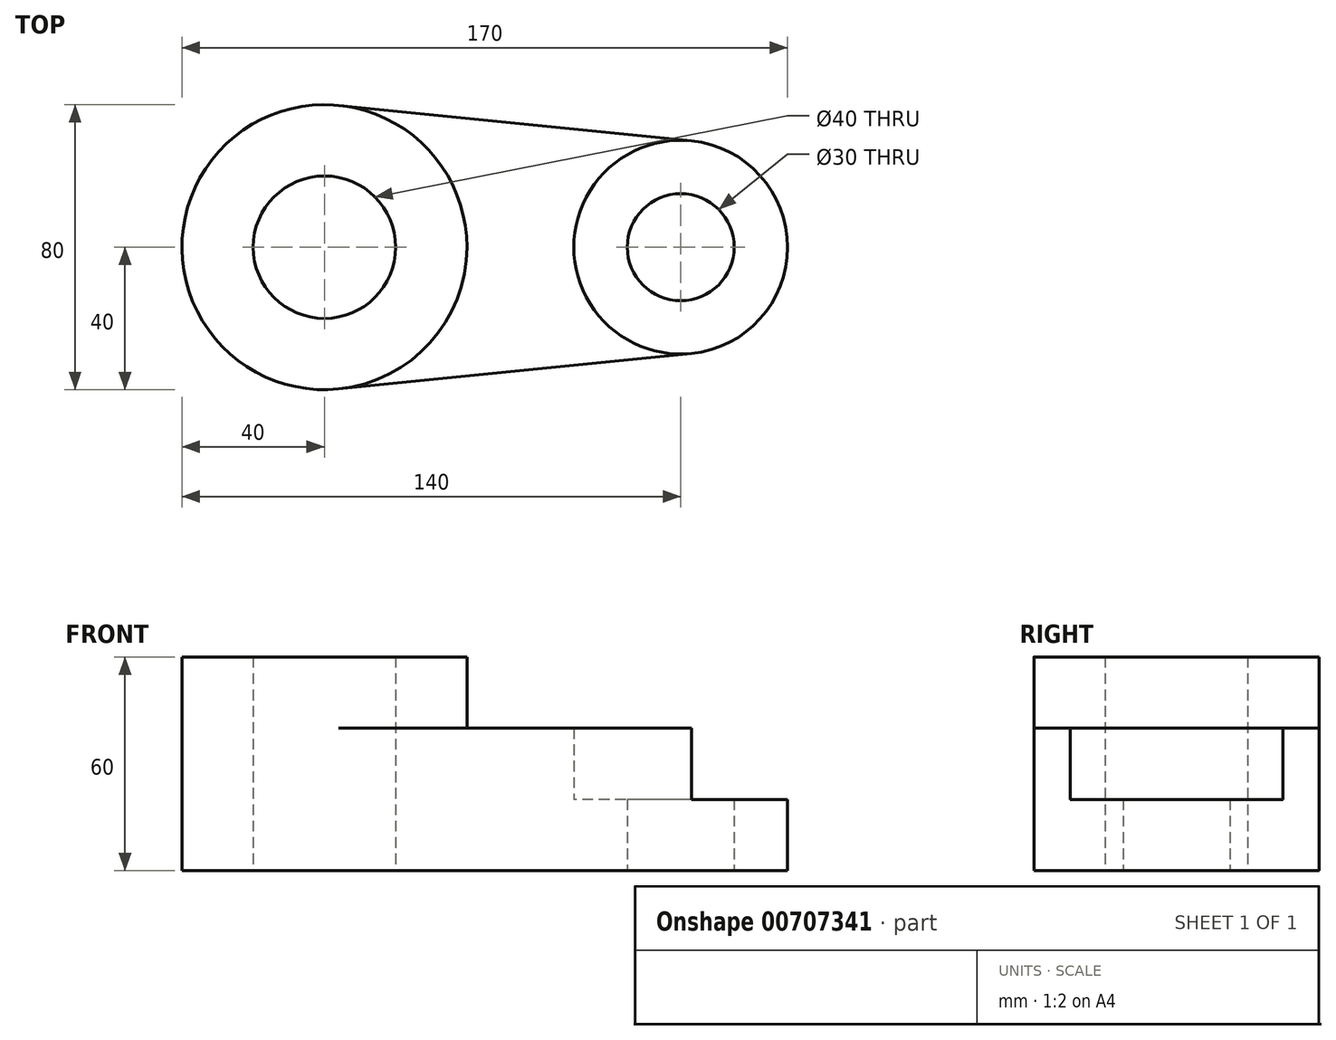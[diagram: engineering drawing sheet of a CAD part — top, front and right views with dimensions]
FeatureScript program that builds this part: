
annotation { "Feature Type Name" : "Feature", "Feature Type Description" : "" }
export const myFeature = defineFeature(function(context is Context, id is Id, definition is map)
    precondition{}
    {
        {
            var Q0;
            Q0=qCreatedBy(makeId("Top.planeOp"),FACE);
            var sketch = newSketch(context, id + "F0", { "sketchPlane" : qUnion([Q0])});
            skCircle(sketch, "E0", {"center": v(-50, 0) * mm, "radius": 20 * mm});
            skCircle(sketch, "E1", {"center": v(-50, 0) * mm, "radius": 40 * mm});
            skCircle(sketch, "E2", {"center": v(50, 0) * mm, "radius": 15 * mm});
            skCircle(sketch, "E3", {"center": v(50, 0) * mm, "radius": 30 * mm});
            skLineSegment(sketch, "E4", {"start": v(-46, -39.8) * mm, "end": v(53, -29.85) * mm});
            skLineSegment(sketch, "E5", {"start": v(-46, 39.8) * mm, "end": v(53, 29.85) * mm});
            skSolve(sketch);
        }
        {
            var Q0;
            Q0=makeQuery(id+"F0.imprint","IMPRINT",FACE,{"disambiguationData":[TD([[makeQuery(id+"F0.imprint","IMPRINT",EDGE,{"derivedFrom":sQuery(id+"F0.wireOp",EDGE,"E0")}),-1.0]])]});
            extrude(context, id + "F1", {"entities" : qUnion([Q0]), "depth" : 60 * mm, "offsetDistance" : 25 * mm});
        }
        {
            var Q0;
            {var subQ0=sQuery(id+"F0.wireOp",EDGE,"E4");Q0=makeQuery(id+"F0.imprint","IMPRINT",FACE,{"disambiguationData":[TD([[makeQuery(id+"F0.imprint","IMPRINT",EDGE,{"derivedFrom":subQ0}),1.0]])]});}
            extrude(context, id + "F2", {"entities" : qUnion([Q0]), "operationType" : NewBodyOperationType.ADD, "depth" : 40 * mm, "offsetDistance" : 25 * mm});
        }
        {
            var Q0;
            Q0=makeQuery(id+"F0.imprint","IMPRINT",FACE,{"disambiguationData":[TD([[makeQuery(id+"F0.imprint","IMPRINT",EDGE,{"derivedFrom":sQuery(id+"F0.wireOp",EDGE,"E2")}),-1.0]])]});
            extrude(context, id + "F3", {"entities" : qUnion([Q0]), "operationType" : NewBodyOperationType.ADD, "depth" : 20 * mm, "offsetDistance" : 25 * mm});
        }
    });
